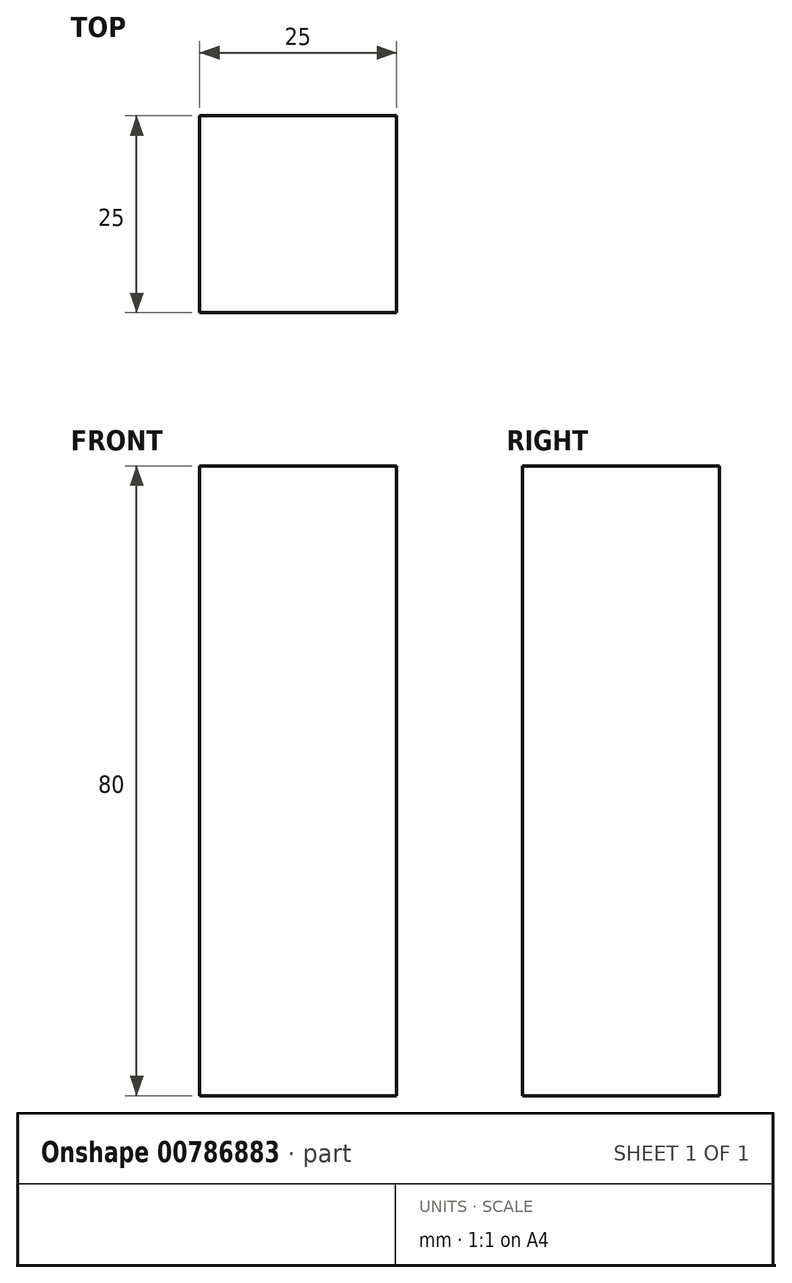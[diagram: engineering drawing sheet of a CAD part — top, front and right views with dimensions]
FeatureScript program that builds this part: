
annotation { "Feature Type Name" : "Feature", "Feature Type Description" : "" }
export const myFeature = defineFeature(function(context is Context, id is Id, definition is map)
    precondition{}
    {
        {
            var Q0;
            Q0=qCreatedBy(makeId("Front.planeOp"),FACE);
            var sketch = newSketch(context, id + "F0", { "sketchPlane" : qUnion([Q0])});
            skLineSegment(sketch, "E0.bottom", {"start": v(-12.5, -27.22) * mm, "end": v(12.5, -27.22) * mm});
            skLineSegment(sketch, "E0.top", {"start": v(-12.5, 52.78) * mm, "end": v(12.5, 52.78) * mm});
            skLineSegment(sketch, "E0.left", {"start": v(-12.5, -27.22) * mm, "end": v(-12.5, 52.78) * mm});
            skLineSegment(sketch, "E0.right", {"start": v(12.5, -27.22) * mm, "end": v(12.5, 52.78) * mm});
            skSolve(sketch);
        }
        {
            var Q0;
            Q0 = qSketchRegion(id + "F0", true);
            extrude(context, id + "F1", {"entities" : qUnion([Q0]), "endBound" : BoundingType.SYMMETRIC, "depth" : 25 * mm, "offsetDistance" : 25 * mm});
        }
    });
